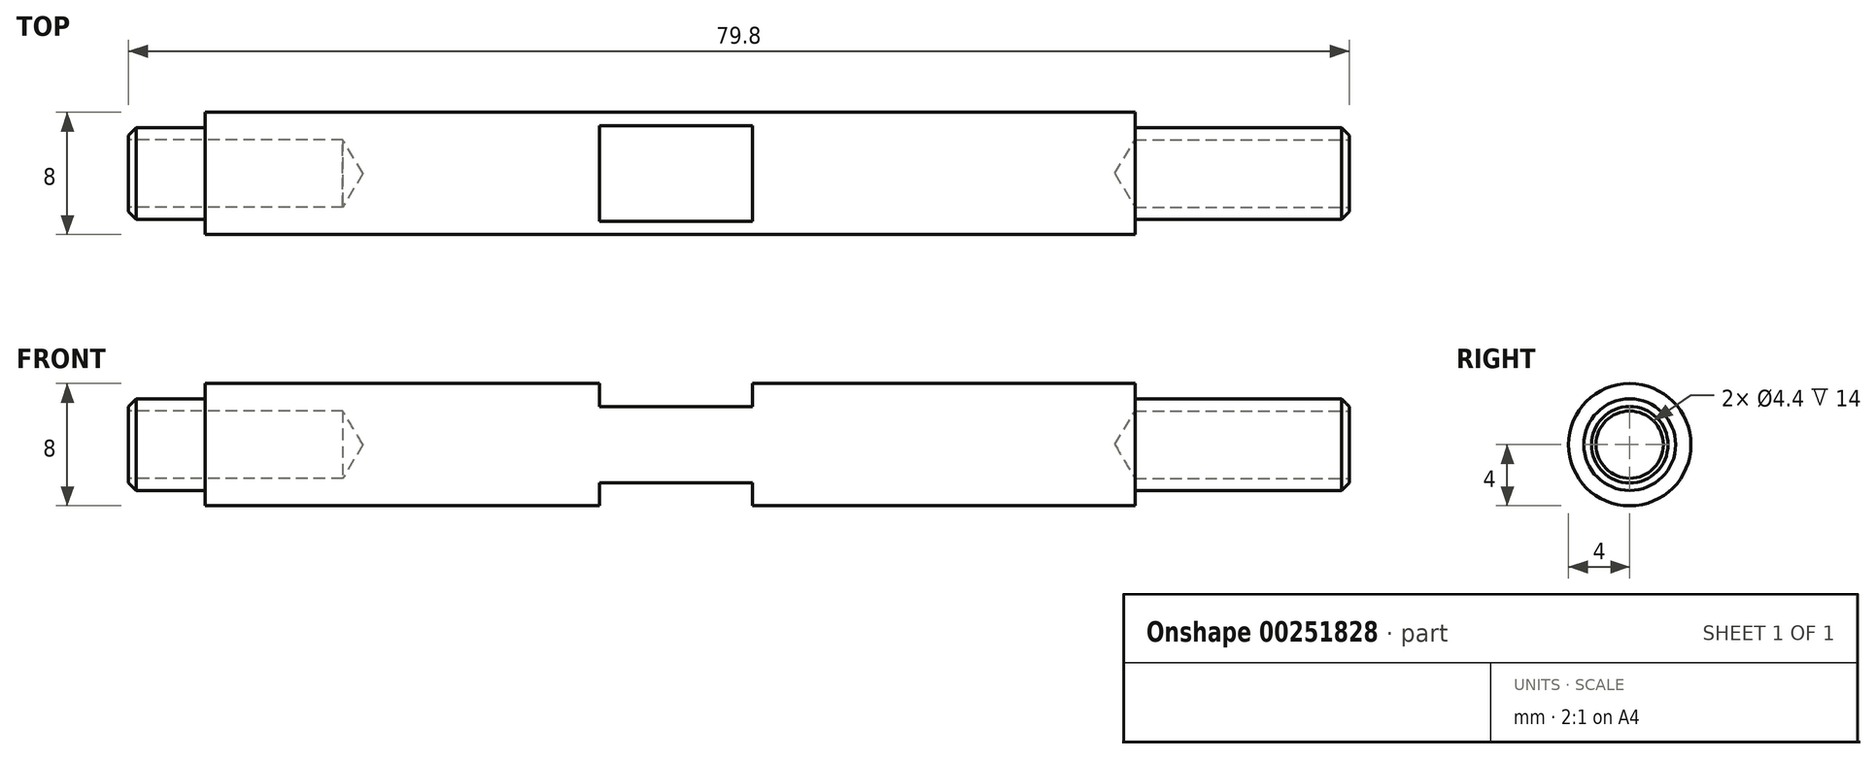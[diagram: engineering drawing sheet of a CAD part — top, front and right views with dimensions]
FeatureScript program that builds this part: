
annotation { "Feature Type Name" : "Feature", "Feature Type Description" : "" }
export const myFeature = defineFeature(function(context is Context, id is Id, definition is map)
    precondition{}
    {
        {
            var Q0;
            Q0=qCreatedBy(makeId("Front.planeOp"),FACE);
            var sketch = newSketch(context, id + "F0", { "sketchPlane" : qUnion([Q0])});
            skLineSegment(sketch, "E0", {"start": v(-48.92, 0) * mm, "end": v(63.67, 0) * mm});
            skLineSegment(sketch, "E1.bottom", {"start": v(-30.4, 4) * mm, "end": v(-5, 4) * mm});
            skLineSegment(sketch, "E1.left", {"start": v(-30.4, 4) * mm, "end": v(-30.4, 0) * mm});
            skLineSegment(sketch, "E1.right", {"start": v(30.4, 4) * mm, "end": v(30.4, 0) * mm});
            skLineSegment(sketch, "E2", {"start": v(0, 8.96) * mm, "end": v(0, -8.78) * mm, "construction": true});
            skPoint(sketch, "E2.endSnap0", {"position": v(0, -4) * mm});
            skLineSegment(sketch, "E3.trimOffspring", {"start": v(5, 4) * mm, "end": v(30.4, 4) * mm});
            skLineSegment(sketch, "E4", {"start": v(-35.4, 0) * mm, "end": v(-35.4, 3) * mm});
            skLineSegment(sketch, "E5", {"start": v(-35.4, 3) * mm, "end": v(-30.4, 3) * mm});
            skPoint(sketch, "E6.orphan", {"position": v(30.4, -4) * mm});
            skPoint(sketch, "E1.top.start.orphan", {"position": v(-30.4, -4) * mm});
            skLineSegment(sketch, "E7", {"start": v(44.4, 0) * mm, "end": v(44.4, 3) * mm});
            skLineSegment(sketch, "E8", {"start": v(44.4, 3) * mm, "end": v(30.4, 3) * mm});
            skLineSegment(sketch, "E9", {"start": v(-5, 4) * mm, "end": v(5, 4) * mm});
            skSolve(sketch);
        }
        {
            var Q0;
            {var subQ4=sQuery(id+"F0.wireOp",EDGE,"E1.bottom");Q0=makeQuery(id+"F0.imprint","IMPRINT",FACE,{"disambiguationData":[TD([[makeQuery(id+"F0.imprint","IMPRINT",EDGE,{"derivedFrom":subQ4}),-1.0]])]});}
            var Q1;
            {var subQ3=sQuery(id+"F0.wireOp",EDGE,"E4");Q1=makeQuery(id+"F0.imprint","IMPRINT",FACE,{"disambiguationData":[TD([[makeQuery(id+"F0.imprint","IMPRINT",EDGE,{"derivedFrom":subQ3}),-1.0]])]});}
            var Q2;
            {var subQ3=sQuery(id+"F0.wireOp",EDGE,"E7");Q2=makeQuery(id+"F0.imprint","IMPRINT",FACE,{"disambiguationData":[TD([[makeQuery(id+"F0.imprint","IMPRINT",EDGE,{"derivedFrom":subQ3}),1.0]])]});}
            var Q3;
            Q3=sQuery(id+"F0.wireOp",EDGE,"E0");
            revolve(context, id + "F1", {"entities" : qUnion([Q0, Q1, Q2]), "axis" : qUnion([Q3]), "revolveType" : RevolveType.FULL});
        }
        {
            var Q0;
            Q0=makeQuery(id+"F1.opRevolve","SWEPT_FACE",FACE,{"disambiguationData":[OSD([sQuery(id+"F0.wireOp",EDGE,"E7")])]});
            var sketch = newSketch(context, id + "F2", { "sketchPlane" : qUnion([Q0])});
            skPoint(sketch, "E10", {"position": v(0, 0) * mm});
            skSolve(sketch);
        }
        {
            var Q0;
            Q0=makeQuery(id+"F1.opRevolve","SWEPT_EDGE",EDGE,{"disambiguationData":[OSD([sQuery(id+"F0.wireOp",EDGE,"E7"),sQuery(id+"F0.wireOp",EDGE,"E8")])]});
            chamfer(context, id + "F3", {"entities" : qUnion([Q0]), "width" : .5 * mm, "tangentPropagation" : true});
        }
        {
            var Q0;
            Q0=sQuery(id+"F2.wireOp",VERTEX,"E10");
            var Q1;
            Q1=makeQuery(id+"F1.opRevolve","SWEPT_BODY",BODY,{"disambiguationData":[OSD([sQuery(id+"F0.wireOp",EDGE,"E0"),sQuery(id+"F0.wireOp",EDGE,"E1.bottom"),sQuery(id+"F0.wireOp",EDGE,"E1.left"),sQuery(id+"F0.wireOp",EDGE,"E1.right"),sQuery(id+"F0.wireOp",EDGE,"E3.trimOffspring"),sQuery(id+"F0.wireOp",EDGE,"E4"),sQuery(id+"F0.wireOp",EDGE,"E5"),sQuery(id+"F0.wireOp",EDGE,"E7"),sQuery(id+"F0.wireOp",EDGE,"E8"),sQuery(id+"F0.wireOp",EDGE,"E9")])]});
            hole(context, id + "F4", {"style" : HoleStyle.SIMPLE, "endStyle" : HoleEndStyle.BLIND, "standardTappedOrClearance" : lookupTablePath({ "standard" : "ISO", "fit" : "Normal", "size" : "M4", "type" : "Clearance" }), "standardBlindInLast" : lookupTablePath({ "fit" : "Standard", "standard" : "ISO", "size" : "M4", "type" : "Clearance" }), "holeDiameter" : 4.4 * mm, "holeDepth" : 14 * mm, "tappedDepth" : 12 * mm, "tapClearance" : 3, "locations" : qUnion([Q0]), "scope" : qUnion([Q1])});
        }
        {
            var Q0;
            Q0=makeQuery(id+"F1.opRevolve","SWEPT_EDGE",EDGE,{"disambiguationData":[OSD([sQuery(id+"F0.wireOp",EDGE,"E4"),sQuery(id+"F0.wireOp",EDGE,"E5")])]});
            chamfer(context, id + "F5", {"entities" : qUnion([Q0]), "width" : .5 * mm, "tangentPropagation" : true});
        }
        {
            var Q0;
            Q0=makeQuery(id+"F1.opRevolve","SWEPT_FACE",FACE,{"disambiguationData":[OSD([sQuery(id+"F0.wireOp",EDGE,"E4")])]});
            var sketch = newSketch(context, id + "F6", { "sketchPlane" : qUnion([Q0])});
            skPoint(sketch, "E11", {"position": v(0, 0) * mm});
            skSolve(sketch);
        }
        {
            var Q0;
            Q0=sQuery(id+"F6.wireOp",VERTEX,"E11");
            var Q1;
            Q1=makeQuery(id+"F1.opRevolve","SWEPT_BODY",BODY,{"disambiguationData":[OSD([sQuery(id+"F0.wireOp",EDGE,"E0"),sQuery(id+"F0.wireOp",EDGE,"E1.bottom"),sQuery(id+"F0.wireOp",EDGE,"E1.left"),sQuery(id+"F0.wireOp",EDGE,"E1.right"),sQuery(id+"F0.wireOp",EDGE,"E3.trimOffspring"),sQuery(id+"F0.wireOp",EDGE,"E4"),sQuery(id+"F0.wireOp",EDGE,"E5"),sQuery(id+"F0.wireOp",EDGE,"E7"),sQuery(id+"F0.wireOp",EDGE,"E8"),sQuery(id+"F0.wireOp",EDGE,"E9")])]});
            hole(context, id + "F7", {"style" : HoleStyle.SIMPLE, "endStyle" : HoleEndStyle.BLIND, "standardTappedOrClearance" : lookupTablePath({ "standard" : "ISO", "fit" : "Normal", "size" : "M4", "type" : "Clearance" }), "standardBlindInLast" : lookupTablePath({ "fit" : "Standard", "standard" : "ISO", "size" : "M4", "type" : "Clearance" }), "holeDiameter" : 4.4 * mm, "holeDepth" : 14 * mm, "tappedDepth" : 12 * mm, "tapClearance" : 3, "locations" : qUnion([Q0]), "scope" : qUnion([Q1])});
        }
        {
            var Q0;
            Q0=qCreatedBy(makeId("Front.planeOp"),FACE);
            var sketch = newSketch(context, id + "F8", { "sketchPlane" : qUnion([Q0])});
            skLineSegment(sketch, "E12", {"start": v(5.4, -4) * mm, "end": v(-4.6, -4) * mm});
            skLineSegment(sketch, "E13", {"start": v(-4.6, -2.5) * mm, "end": v(5.4, -2.5) * mm});
            skLineSegment(sketch, "E14", {"start": v(5.4, -2.5) * mm, "end": v(5.4, -4) * mm});
            skLineSegment(sketch, "E15", {"start": v(-4.6, -2.5) * mm, "end": v(-4.6, -4) * mm});
            skLineSegment(sketch, "E16.MirrorCS", {"start": v(5.4, 4) * mm, "end": v(-4.6, 4) * mm});
            skLineSegment(sketch, "E17.MirrorCS", {"start": v(-4.6, 2.5) * mm, "end": v(5.4, 2.5) * mm});
            skLineSegment(sketch, "E18.MirrorCS", {"start": v(5.4, 2.5) * mm, "end": v(5.4, 4) * mm});
            skLineSegment(sketch, "E19.MirrorCS", {"start": v(-4.6, 2.5) * mm, "end": v(-4.6, 4) * mm});
            skPoint(sketch, "E20.orphan", {"position": v(-30.4, -4) * mm});
            skPoint(sketch, "E21.orphan", {"position": v(30.4, -4) * mm});
            skPoint(sketch, "E22.orphan", {"position": v(30.4, 4) * mm});
            skPoint(sketch, "E23.orphan", {"position": v(-30.4, 4) * mm});
            skSolve(sketch);
        }
        {
            var Q0;
            Q0 = qSketchRegion(id + "F8", true);
            extrude(context, id + "F9", {"entities" : qUnion([Q0]), "operationType" : NewBodyOperationType.REMOVE, "endBound" : BoundingType.SYMMETRIC, "oppositeDirection" : true, "depth" : 20 * mm});
        }
    });
